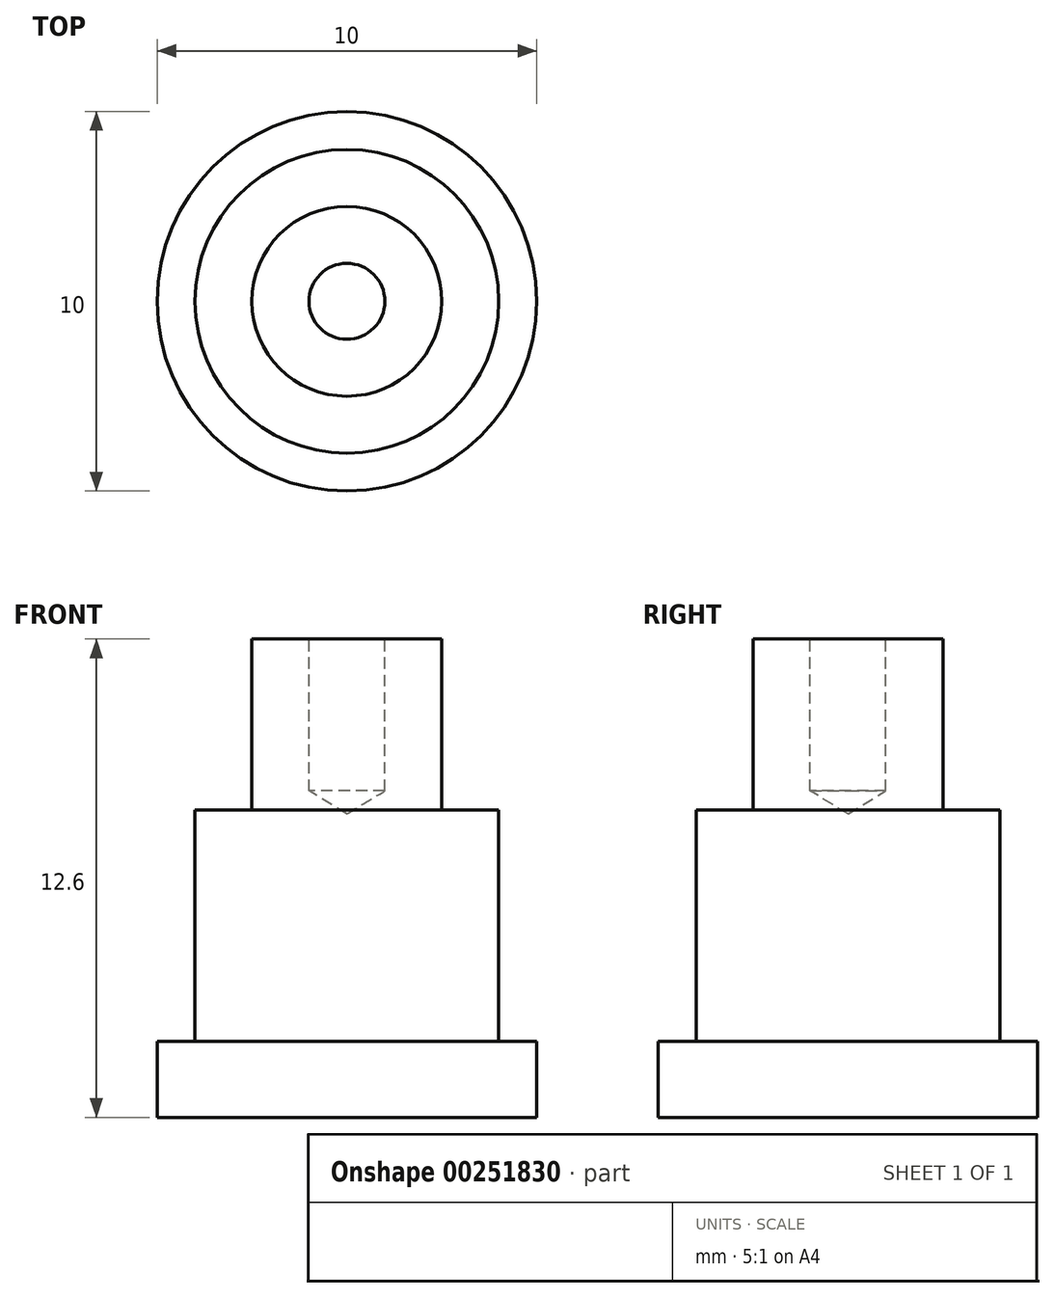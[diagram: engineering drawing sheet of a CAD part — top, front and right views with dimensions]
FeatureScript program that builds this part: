
annotation { "Feature Type Name" : "Feature", "Feature Type Description" : "" }
export const myFeature = defineFeature(function(context is Context, id is Id, definition is map)
    precondition{}
    {
        {
            var Q0;
            Q0=qCreatedBy(makeId("Top.planeOp"),FACE);
            var sketch = newSketch(context, id + "F0", { "sketchPlane" : qUnion([Q0])});
            skCircle(sketch, "E0", {"center": v(0, 0) * mm, "radius": 5 * mm});
            skSolve(sketch);
        }
        {
            var Q0;
            Q0=makeQuery(id+"F0.imprint","IMPRINT",FACE,{"disambiguationData":[TD([[makeQuery(id+"F0.imprint","IMPRINT",EDGE,{"derivedFrom":sQuery(id+"F0.wireOp",EDGE,"E0")}),1.0]])]});
            extrude(context, id + "F1", {"entities" : qUnion([Q0]), "depth" : 2 * mm});
        }
        {
            var Q0;
            Q0=makeQuery(id+"F1.opExtrude","CAP_FACE",FACE,{"disambiguationData":[OSD([sQuery(id+"F0.wireOp",EDGE,"E0")])],"isStart":false});
            var sketch = newSketch(context, id + "F2", { "sketchPlane" : qUnion([Q0])});
            skCircle(sketch, "E1", {"center": v(0, 0) * mm, "radius": 4 * mm});
            skSolve(sketch);
        }
        {
            var Q0;
            Q0 = qSketchRegion(id + "F2", true);
            extrude(context, id + "F3", {"entities" : qUnion([Q0]), "operationType" : NewBodyOperationType.ADD, "depth" : 6.1 * mm});
        }
        {
            var Q0;
            Q0=makeQuery(id+"F3.opExtrude","CAP_FACE",FACE,{"disambiguationData":[OSD([sQuery(id+"F2.wireOp",EDGE,"E1")])],"isStart":false});
            var sketch = newSketch(context, id + "F4", { "sketchPlane" : qUnion([Q0])});
            skCircle(sketch, "E2", {"center": v(0, 0) * mm, "radius": 2.5 * mm});
            skSolve(sketch);
        }
        {
            var Q0;
            Q0=makeQuery(id+"F4.imprint","IMPRINT",FACE,{"disambiguationData":[TD([[makeQuery(id+"F4.imprint","IMPRINT",EDGE,{"derivedFrom":sQuery(id+"F4.wireOp",EDGE,"E2")}),1.0]])]});
            extrude(context, id + "F5", {"entities" : qUnion([Q0]), "operationType" : NewBodyOperationType.ADD, "depth" : 4.5 * mm});
        }
        {
            var Q0;
            Q0=makeQuery(id+"F5.opExtrude","CAP_FACE",FACE,{"disambiguationData":[OSD([sQuery(id+"F4.wireOp",EDGE,"E2")])],"isStart":false});
            var sketch = newSketch(context, id + "F6", { "sketchPlane" : qUnion([Q0])});
            skPoint(sketch, "E3", {"position": v(0, 0) * mm});
            skSolve(sketch);
        }
        {
            var Q0;
            Q0=sQuery(id+"F6.wireOp",VERTEX,"E3");
            var Q1;
            Q1=makeQuery(id+"F1.opExtrude","SWEPT_BODY",BODY,{"disambiguationData":[OSD([sQuery(id+"F0.wireOp",EDGE,"E0")])]});
            hole(context, id + "F7", {"style" : HoleStyle.SIMPLE, "endStyle" : HoleEndStyle.BLIND, "holeDiameter" : 2 * mm, "holeDepth" : 4 * mm, "tappedDepth" : 12 * mm, "tapClearance" : 3, "locations" : qUnion([Q0]), "scope" : qUnion([Q1])});
        }
    });
